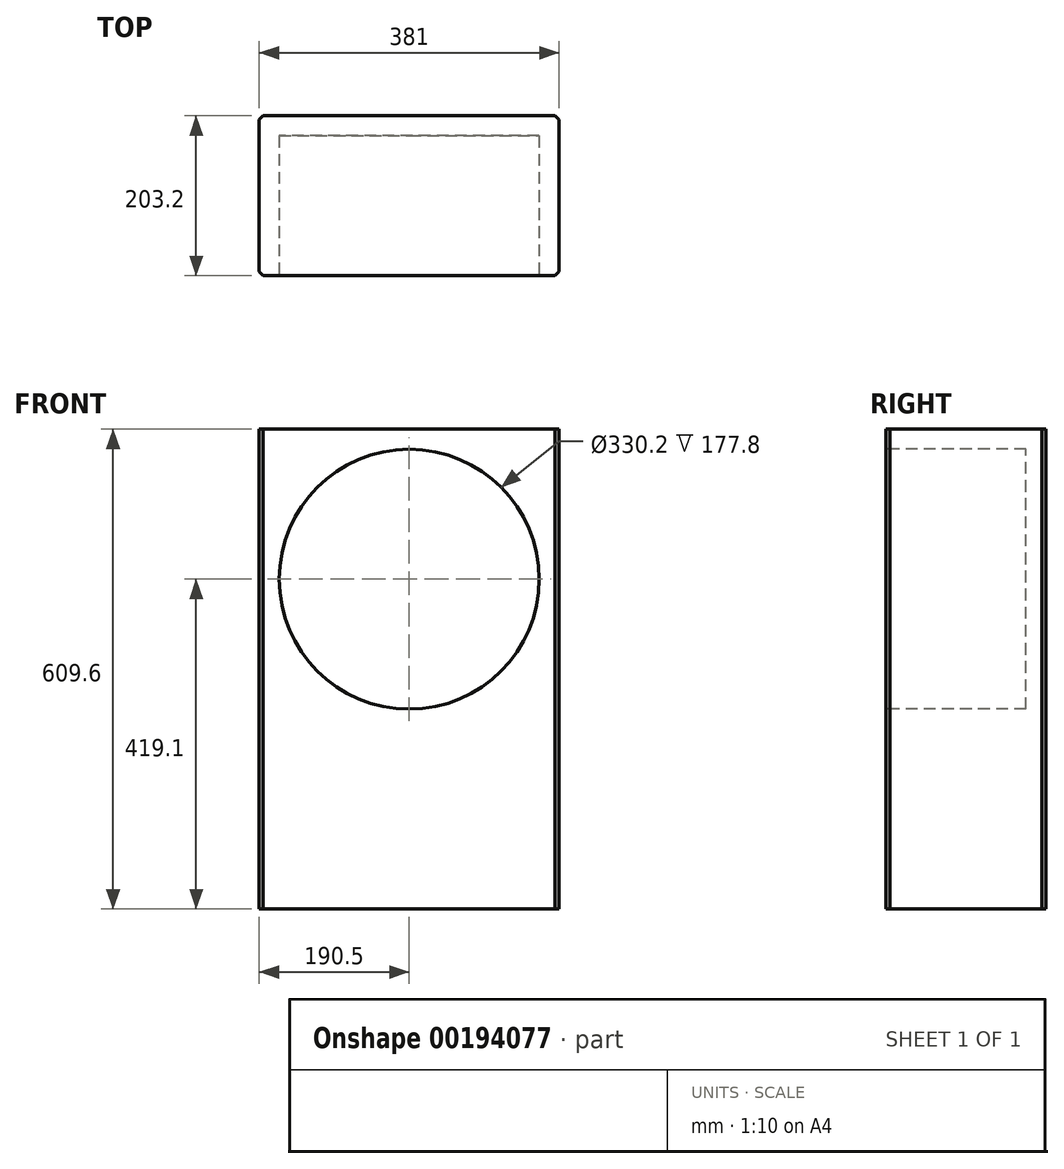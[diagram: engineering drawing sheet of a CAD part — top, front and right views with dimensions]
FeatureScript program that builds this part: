
annotation { "Feature Type Name" : "Feature", "Feature Type Description" : "" }
export const myFeature = defineFeature(function(context is Context, id is Id, definition is map)
    precondition{}
    {
        {
            var Q0;
            Q0=qCreatedBy(makeId("Top.planeOp"),FACE);
            var sketch = newSketch(context, id + "F0", { "sketchPlane" : qUnion([Q0])});
            skLineSegment(sketch, "E0.bottom", {"start": v(0, 0) * mm, "end": v(381, 0) * mm});
            skLineSegment(sketch, "E0.top", {"start": v(0, 203.2) * mm, "end": v(381, 203.2) * mm});
            skLineSegment(sketch, "E0.left", {"start": v(0, 0) * mm, "end": v(0, 203.2) * mm});
            skLineSegment(sketch, "E0.right", {"start": v(381, 0) * mm, "end": v(381, 203.2) * mm});
            skSolve(sketch);
        }
        {
            var Q0;
            Q0=makeQuery(id+"F0.imprint","IMPRINT",FACE,{"disambiguationData":[TD([[makeQuery(id+"F0.imprint","IMPRINT",EDGE,{"derivedFrom":sQuery(id+"F0.wireOp",EDGE,"E0.bottom")}),1.0]])]});
            extrude(context, id + "F1", {"entities" : qUnion([Q0]), "depth" : 609.6 * mm});
        }
        {
            var Q0;
            Q0=makeQuery(id+"F1.opExtrude","SWEPT_FACE",FACE,{"disambiguationData":[OSD([sQuery(id+"F0.wireOp",EDGE,"E0.bottom")])]});
            var sketch = newSketch(context, id + "F2", { "sketchPlane" : qUnion([Q0])});
            skLineSegment(sketch, "E1", {"start": v(0, 609.6) * mm, "end": v(0, 228.6) * mm, "construction": true});
            skLineSegment(sketch, "E2", {"start": v(0, 228.6) * mm, "end": v(381, 228.6) * mm, "construction": true});
            skLineSegment(sketch, "E3", {"start": v(381, 228.6) * mm, "end": v(0, 609.6) * mm, "construction": true});
            skLineSegment(sketch, "E4", {"start": v(381, 609.6) * mm, "end": v(0, 228.6) * mm, "construction": true});
            skPoint(sketch, "E5", {"position": v(190.5, 419.1) * mm});
            skCircle(sketch, "E6", {"center": v(190.5, 419.1) * mm, "radius": 165.1 * mm});
            skSolve(sketch);
        }
        {
            var Q0;
            Q0=makeQuery(id+"F2.imprint","IMPRINT",FACE,{"disambiguationData":[TD([[makeQuery(id+"F2.imprint","IMPRINT",EDGE,{"derivedFrom":sQuery(id+"F2.wireOp",EDGE,"E6")}),1.0]])]});
            var Q1;
            Q1=makeQuery(id+"F1.opExtrude","SWEPT_FACE",FACE,{"disambiguationData":[OSD([sQuery(id+"F0.wireOp",EDGE,"E0.top")])]});
            extrude(context, id + "F3", {"entities" : qUnion([Q0]), "operationType" : NewBodyOperationType.REMOVE, "oppositeDirection" : true, "endBoundEntityFace" : qUnion([Q1]), "depth" : 177.8 * mm});
        }
        {
            var Q0;
            Q0=makeQuery(id+"F1.opExtrude","SWEPT_EDGE",EDGE,{"disambiguationData":[OSD([sQuery(id+"F0.wireOp",EDGE,"E0.top"),sQuery(id+"F0.wireOp",EDGE,"E0.left")])]});
            var Q1;
            Q1=makeQuery(id+"F1.opExtrude","SWEPT_EDGE",EDGE,{"disambiguationData":[OSD([sQuery(id+"F0.wireOp",EDGE,"E0.bottom"),sQuery(id+"F0.wireOp",EDGE,"E0.left")])]});
            var Q2;
            Q2=makeQuery(id+"F1.opExtrude","SWEPT_EDGE",EDGE,{"disambiguationData":[OSD([sQuery(id+"F0.wireOp",EDGE,"E0.bottom"),sQuery(id+"F0.wireOp",EDGE,"E0.right")])]});
            var Q3;
            Q3=makeQuery(id+"F1.opExtrude","SWEPT_EDGE",EDGE,{"disambiguationData":[OSD([sQuery(id+"F0.wireOp",EDGE,"E0.top"),sQuery(id+"F0.wireOp",EDGE,"E0.right")])]});
            chamfer(context, id + "F4", {"entities" : qUnion([Q0, Q1, Q2, Q3]), "width" : 5.08 * mm, "tangentPropagation" : true});
        }
    });
